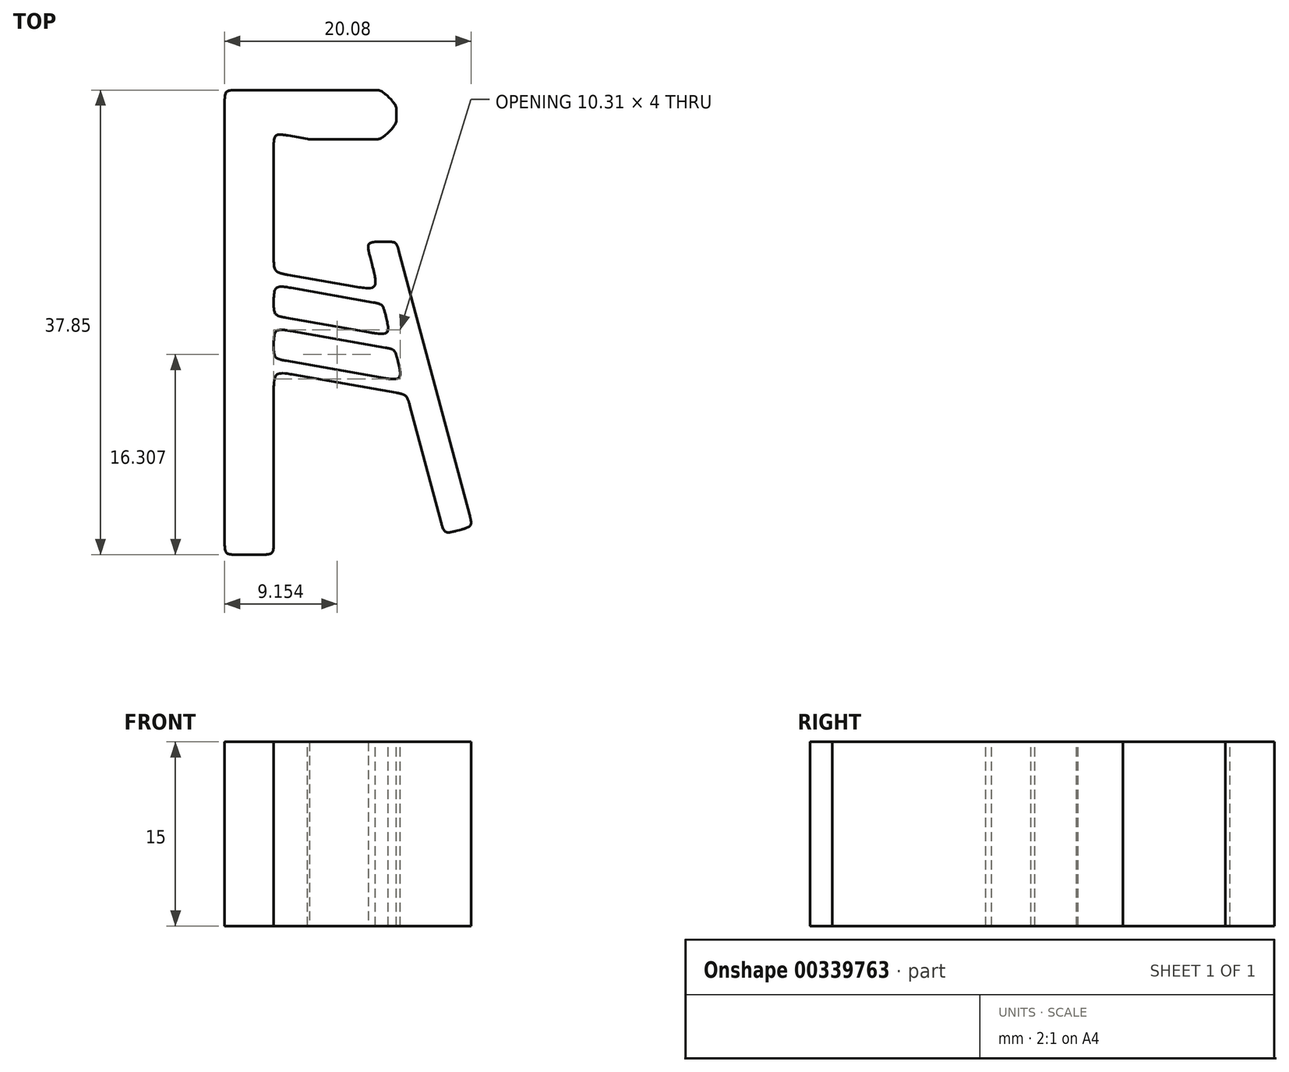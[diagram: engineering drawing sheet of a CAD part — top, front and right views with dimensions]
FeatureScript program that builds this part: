
annotation { "Feature Type Name" : "Feature", "Feature Type Description" : "" }
export const myFeature = defineFeature(function(context is Context, id is Id, definition is map)
    precondition{}
    {
        {
            var Q0;
            Q0=qCreatedBy(makeId("Top.planeOp"),FACE);
            var sketch = newSketch(context, id + "F0", { "sketchPlane" : qUnion([Q0])});
            skLineSegment(sketch, "E0", {"start": v(0, 0) * mm, "end": v(35.88, 0) * mm});
            skLineSegment(sketch, "E1", {"start": v(0, 0) * mm, "end": v(0, 8.85) * mm});
            skLineSegment(sketch, "E2", {"start": v(0, 8.85) * mm, "end": v(36.04, 8.85) * mm});
            skSolve(sketch);
        }
        {
            var Q0;
            Q0=qCreatedBy(makeId("Top.planeOp"),FACE);
            var sketch = newSketch(context, id + "F1", { "sketchPlane" : qUnion([Q0])});
            skLineSegment(sketch, "E3", {"start": v(2.84, 8.85) * mm, "end": v(10, 8.85) * mm});
            skLineSegment(sketch, "E4", {"start": v(10, 8.85) * mm, "end": v(10, 12.85) * mm});
            skLineSegment(sketch, "E5", {"start": v(10, 12.85) * mm, "end": v(-4, 12.85) * mm});
            skLineSegment(sketch, "E6", {"start": v(-4, 12.85) * mm, "end": v(-4, -25) * mm});
            skLineSegment(sketch, "E7", {"start": v(2.84, 8.85) * mm, "end": v(0, 9.35) * mm});
            skLineSegment(sketch, "E8", {"start": v(0, 9.35) * mm, "end": v(0, -2) * mm});
            skLineSegment(sketch, "E9", {"start": v(0, -9.03) * mm, "end": v(10.57, -10.9) * mm});
            skLineSegment(sketch, "E10", {"start": v(10.57, -10.9) * mm, "end": v(9.87, -8.27) * mm});
            skLineSegment(sketch, "E11", {"start": v(10, 0.5) * mm, "end": v(16.22, -22.7) * mm});
            skLineSegment(sketch, "E12", {"start": v(16.22, -22.7) * mm, "end": v(13.9, -23.33) * mm});
            skLineSegment(sketch, "E13", {"start": v(13.9, -23.33) * mm, "end": v(10.85, -11.96) * mm});
            skLineSegment(sketch, "E14", {"start": v(10.85, -11.96) * mm, "end": v(0, -10.05) * mm});
            skLineSegment(sketch, "E15", {"start": v(0, -10.05) * mm, "end": v(0, -25) * mm});
            skLineSegment(sketch, "E16", {"start": v(0, -25) * mm, "end": v(-4, -25) * mm});
            skArc(sketch, "E17", {"start": v(0, -25) * mm, "mid": v(7.12, -25.55) * mm, "end": v(13.9, -23.33) * mm, "construction": true});
            skLineSegment(sketch, "E18", {"start": v(7.52, 0.5) * mm, "end": v(10, 0.5) * mm});
            skLineSegment(sketch, "E19", {"start": v(0, -6.53) * mm, "end": v(9.87, -8.27) * mm});
            skLineSegment(sketch, "E20", {"start": v(0, -5.52) * mm, "end": v(9.58, -7.2) * mm});
            skLineSegment(sketch, "E21", {"start": v(0, -3.02) * mm, "end": v(8.88, -4.58) * mm});
            skLineSegment(sketch, "E22", {"start": v(0, -2) * mm, "end": v(8.6, -3.51) * mm});
            skLineSegment(sketch, "E23.trimOffspring", {"start": v(0, -3.02) * mm, "end": v(0, -5.52) * mm});
            skLineSegment(sketch, "E24.trimOffspring", {"start": v(0, -6.53) * mm, "end": v(0, -9.03) * mm});
            skLineSegment(sketch, "E25.trimOffspring", {"start": v(9.58, -7.2) * mm, "end": v(8.88, -4.58) * mm});
            skLineSegment(sketch, "E26.trimOffspring", {"start": v(8.6, -3.51) * mm, "end": v(7.52, 0.5) * mm});
            skLineSegment(sketch, "E27", {"start": v(8.6, -3.51) * mm, "end": v(8.42, -4.5) * mm, "construction": true});
            skLineSegment(sketch, "E28", {"start": v(9.58, -7.2) * mm, "end": v(9.4, -8.19) * mm, "construction": true});
            skLineSegment(sketch, "E29", {"start": v(10.57, -10.9) * mm, "end": v(10.4, -11.88) * mm});
            skSolve(sketch);
        }
        {
            var Q0;
            Q0 = qSketchRegion(id + "F1", true);
            extrude(context, id + "F2", {"entities" : qUnion([Q0]), "endBound" : BoundingType.SYMMETRIC, "depth" : 15 * mm});
        }
        {
            var Q0;
            Q0=makeQuery(id+"F2.opExtrude","SWEPT_EDGE",EDGE,{"disambiguationData":[OSD([sQuery(id+"F1.wireOp",EDGE,"E4"),sQuery(id+"F1.wireOp",EDGE,"E5")])]});
            var Q1;
            Q1=makeQuery(id+"F2.opExtrude","SWEPT_EDGE",EDGE,{"disambiguationData":[OSD([sQuery(id+"F1.wireOp",EDGE,"E3"),sQuery(id+"F1.wireOp",EDGE,"E4")])]});
            fillet(context, id + "F3", {"entities" : qUnion([Q0, Q1]), "radius" : 1.5 * mm, "tangentPropagation" : true, "rho" : .2, "crossSection" : FilletCrossSection.CONIC, "allowEdgeOverflow" : false});
        }
        {
            var Q0;
            Q0=makeQuery(id+"F2.opExtrude","SWEPT_EDGE",EDGE,{"disambiguationData":[OSD([sQuery(id+"F1.wireOp",EDGE,"E11"),sQuery(id+"F1.wireOp",EDGE,"E18")])]});
            var Q1;
            Q1=makeQuery(id+"F2.opExtrude","SWEPT_EDGE",EDGE,{"disambiguationData":[OSD([sQuery(id+"F1.wireOp",EDGE,"E18"),sQuery(id+"F1.wireOp",EDGE,"E26.trimOffspring")])]});
            var Q2;
            Q2=makeQuery(id+"F2.opExtrude","SWEPT_EDGE",EDGE,{"disambiguationData":[OSD([sQuery(id+"F1.wireOp",EDGE,"E7"),sQuery(id+"F1.wireOp",EDGE,"E8")])]});
            var Q3;
            Q3=makeQuery(id+"F2.opExtrude","SWEPT_EDGE",EDGE,{"disambiguationData":[OSD([sQuery(id+"F1.wireOp",EDGE,"E3"),sQuery(id+"F1.wireOp",EDGE,"E7")])]});
            var Q4;
            Q4=makeQuery(id+"F2.opExtrude","SWEPT_EDGE",EDGE,{"disambiguationData":[OSD([sQuery(id+"F1.wireOp",EDGE,"E11"),sQuery(id+"F1.wireOp",EDGE,"E12")])]});
            var Q5;
            Q5=makeQuery(id+"F2.opExtrude","SWEPT_EDGE",EDGE,{"disambiguationData":[OSD([sQuery(id+"F1.wireOp",EDGE,"E12"),sQuery(id+"F1.wireOp",EDGE,"E13")])]});
            var Q6;
            Q6=makeQuery(id+"F2.opExtrude","SWEPT_EDGE",EDGE,{"disambiguationData":[OSD([sQuery(id+"F1.wireOp",EDGE,"E15"),sQuery(id+"F1.wireOp",EDGE,"E16")])]});
            var Q7;
            Q7=makeQuery(id+"F2.opExtrude","SWEPT_EDGE",EDGE,{"disambiguationData":[OSD([sQuery(id+"F1.wireOp",EDGE,"E6"),sQuery(id+"F1.wireOp",EDGE,"E16")])]});
            var Q8;
            Q8=makeQuery(id+"F2.opExtrude","SWEPT_EDGE",EDGE,{"disambiguationData":[OSD([sQuery(id+"F1.wireOp",EDGE,"E5"),sQuery(id+"F1.wireOp",EDGE,"E6")])]});
            var Q9;
            Q9=makeQuery(id+"F2.opExtrude","SWEPT_EDGE",EDGE,{"disambiguationData":[OSD([sQuery(id+"F1.wireOp",EDGE,"E11"),sQuery(id+"F1.wireOp",EDGE,"E18")])]});
            fillet(context, id + "F4", {"entities" : qUnion([Q0, Q1, Q2, Q3, Q4, Q5, Q6, Q7, Q8, Q9]), "radius" : 1 * mm, "tangentPropagation" : true, "rho" : .7, "crossSection" : FilletCrossSection.CONIC, "allowEdgeOverflow" : false});
        }
        {
            var Q0;
            Q0=makeQuery(id+"F2.opExtrude","SWEPT_EDGE",EDGE,{"disambiguationData":[OSD([sQuery(id+"F1.wireOp",EDGE,"E8"),sQuery(id+"F1.wireOp",EDGE,"E22")])]});
            var Q1;
            Q1=makeQuery(id+"F2.opExtrude","SWEPT_EDGE",EDGE,{"disambiguationData":[OSD([sQuery(id+"F1.wireOp",EDGE,"E14"),sQuery(id+"F1.wireOp",EDGE,"E15")])]});
            var Q2;
            Q2=makeQuery(id+"F2.opExtrude","SWEPT_EDGE",EDGE,{"disambiguationData":[OSD([sQuery(id+"F1.wireOp",EDGE,"E13"),sQuery(id+"F1.wireOp",EDGE,"E14")])]});
            var Q3;
            Q3=makeQuery(id+"F2.opExtrude","SWEPT_EDGE",EDGE,{"disambiguationData":[OSD([sQuery(id+"F1.wireOp",EDGE,"E22"),sQuery(id+"F1.wireOp",EDGE,"E26.trimOffspring")])]});
            fillet(context, id + "F5", {"entities" : qUnion([Q0, Q1, Q2, Q3]), "radius" : 1.4 * mm, "tangentPropagation" : true, "rho" : 0.7, "crossSection" : FilletCrossSection.CONIC, "allowEdgeOverflow" : false});
        }
        {
            var Q0;
            Q0=makeQuery(id+"F2.opExtrude","SWEPT_EDGE",EDGE,{"disambiguationData":[OSD([sQuery(id+"F1.wireOp",EDGE,"E10"),sQuery(id+"F1.wireOp",EDGE,"E19")])]});
            var Q1;
            Q1=makeQuery(id+"F2.opExtrude","SWEPT_EDGE",EDGE,{"disambiguationData":[OSD([sQuery(id+"F1.wireOp",EDGE,"E21"),sQuery(id+"F1.wireOp",EDGE,"E23.trimOffspring")])]});
            var Q2;
            Q2=makeQuery(id+"F2.opExtrude","SWEPT_EDGE",EDGE,{"disambiguationData":[OSD([sQuery(id+"F1.wireOp",EDGE,"E19"),sQuery(id+"F1.wireOp",EDGE,"E24.trimOffspring")])]});
            var Q3;
            Q3=makeQuery(id+"F2.opExtrude","SWEPT_EDGE",EDGE,{"disambiguationData":[OSD([sQuery(id+"F1.wireOp",EDGE,"E20"),sQuery(id+"F1.wireOp",EDGE,"E25.trimOffspring")])]});
            var Q4;
            Q4=makeQuery(id+"F2.opExtrude","SWEPT_EDGE",EDGE,{"disambiguationData":[OSD([sQuery(id+"F1.wireOp",EDGE,"E9"),sQuery(id+"F1.wireOp",EDGE,"E10")])]});
            var Q5;
            Q5=makeQuery(id+"F2.opExtrude","SWEPT_EDGE",EDGE,{"disambiguationData":[OSD([sQuery(id+"F1.wireOp",EDGE,"E9"),sQuery(id+"F1.wireOp",EDGE,"E24.trimOffspring")])]});
            var Q6;
            Q6=makeQuery(id+"F2.opExtrude","SWEPT_EDGE",EDGE,{"disambiguationData":[OSD([sQuery(id+"F1.wireOp",EDGE,"E20"),sQuery(id+"F1.wireOp",EDGE,"E23.trimOffspring")])]});
            var Q7;
            Q7=makeQuery(id+"F2.opExtrude","SWEPT_EDGE",EDGE,{"disambiguationData":[OSD([sQuery(id+"F1.wireOp",EDGE,"E21"),sQuery(id+"F1.wireOp",EDGE,"E25.trimOffspring")])]});
            fillet(context, id + "F6", {"entities" : qUnion([Q0, Q1, Q2, Q3, Q4, Q5, Q6, Q7]), "radius" : 1.2 * mm, "tangentPropagation" : true, "rho" : .7, "crossSection" : FilletCrossSection.CONIC, "allowEdgeOverflow" : false});
        }
    });
